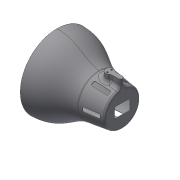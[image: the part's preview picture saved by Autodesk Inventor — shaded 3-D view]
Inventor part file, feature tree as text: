
AUTODESK INVENTOR PART (.ipt)
format: ipt  version: 2018 (Build 220112000, 112)  size: 549,376 bytes
history: native  units: mm
features: fillet x8, sketch x5, extrude x4, projected_geometry x2, revolve x1, shell x1, plane x1, hole x1, pattern_circular x1
ambient origin geometry x8: Origin, YZ Plane, XZ Plane, XY Plane, X Axis, Y Axis, Z Axis, Center Point
bodies: Solid1 (feature_tree)
feature tree (24):
  revolve  "Revolution1"  [1 undecoded]
  fillet  "Fillet1"  Radius=45.0mm
  shell  "Shell1"  Thickness=45.0mm
  fillet  "Fillet3"  Radius=10.0mm
  plane  "Work Plane1"
  extrude  "Extrusion1"  Depth=22.0mm
  hole  "Hole1"  [1 undecoded]
  extrude  "Extrusion3"  Depth=1.0mm
  fillet  "Fillet4"  Radius=1.0mm
  pattern_circular  "Circular Pattern1"  Count=5  [1 undecoded]
  extrude  "Extrusion4"  Depth=3.0mm
  fillet  "Fillet5"  Radius=38.0mm
  fillet  "Fillet6"  Radius=10.0mm
  fillet  "Fillet7"  Radius=8.0mm
  fillet  "Fillet8"  Radius=30.0mm
  extrude  "Extrusion5"  Depth=3.0mm
  fillet  "Fillet9"  Radius=40.0mm
  sketch  "Sketch1"  dims[d0=125.0mm d1=40.0mm d2=45.0mm d3=45.0mm d4=10.0mm]
  sketch  "Sketch2"  dims[d5=70.0mm d6=22.0mm]
  sketch  "Sketch4"  dims[d7=70.0mm d8=90.0deg]
  projected_geometry  "Projected Loop2"
  sketch  "Sketch5"  dims[d9=17.104227mm d10=25.0mm d12=1.0mm]
  sketch  "Sketch6"  dims[d13=0.25mm d14=50.0mm d15=15.0mm d16=38.0mm d17=10.0mm d18=0.0mm d22=8.0mm d23=3.2mm d24=6.0mm d25=6.3mm d26=2.0mm d27=90.0deg d28=15.0mm d29=20.594885mm d30=30.0mm d31=8.0mm d32=40.0mm d33=0.0mm d34=0.0mm d35=2.0mm d36=60.0mm d37=360.0deg d39=20.0mm d40=10.0mm d41=0.0mm d42=8.0mm d43=8.0mm d44=3.0mm d45=3.5mm d55=17.0mm d56=30.0mm d57=10.0mm d58=0.0mm d59=3.0mm d60=3.0mm]
  projected_geometry  "Projected Loop3"
note: 3 required parameter values undecoded (feature->parameter linkage not recoverable at this tier; creation-order binding heuristic only, values carry confidence <= 0.55)